# Revit family: CSL
name_source: partatom
category: Lighting Fixtures
units: mm (PartAtom-declared; Revit-internal decimal feet)

## family parameters
Cut with Voids When Loaded = No
Host = Face
Light Source = Yes
OmniClass Number = 23.80.70.11
OmniClass Title = Luminaries for Internal Lighting
Part Type = Normal
Room Calculation Point = No
Round Connector Dimension = Use Diameter
Shared = No

## types (4) — shared parameters
Backbox = White
Color Filter = 16777215
Default Elevation = 4' - 0"
Description = LED Striplight
Dimming = 0-10V
Dimming Lamp Color Temperature Shift = <None>
Emit Shape Visible in Rendering = No
Emit from Rectangle Width = 0' - 2 1/2"
Glass = White Glass
Lamp = LED Lamp
Load Classification = Lighting
Manufacturer = Columbia Lighting
Model = CSL4
Mounting = Surface mount on wall or ceiling
Photometric Web File = generic.ies
Power Factor = 1
Tilt Angle = -90.00°
URL = https://www.currentlighting.com
Voltage = 120 V
Warranty = Five Year Warranty
Wattage Comments = 40.2W-80.5W

## per-type parameters (varying)
| type | Apparent Load | Emit from Rectangle Length | Row Length | Watts |
| CSL4-4035 | 40 VA | 3' - 11 1/2" | 4' - 0" | 40 W |
| CSL4-4040 | 40 VA | 3' - 11 1/2" | 4' - 0" | 40 W |
| CSL8-8035 | 81 VA | 7' - 11 1/2" | 8' - 0" | 81 W |
| CSL8-8040 | 81 VA | 7' - 11 1/2" | 8' - 0" | 81 W |

## geometry (parser evidence)
native form markers: Sweep x3
no freeform markers — native parametric forms only
